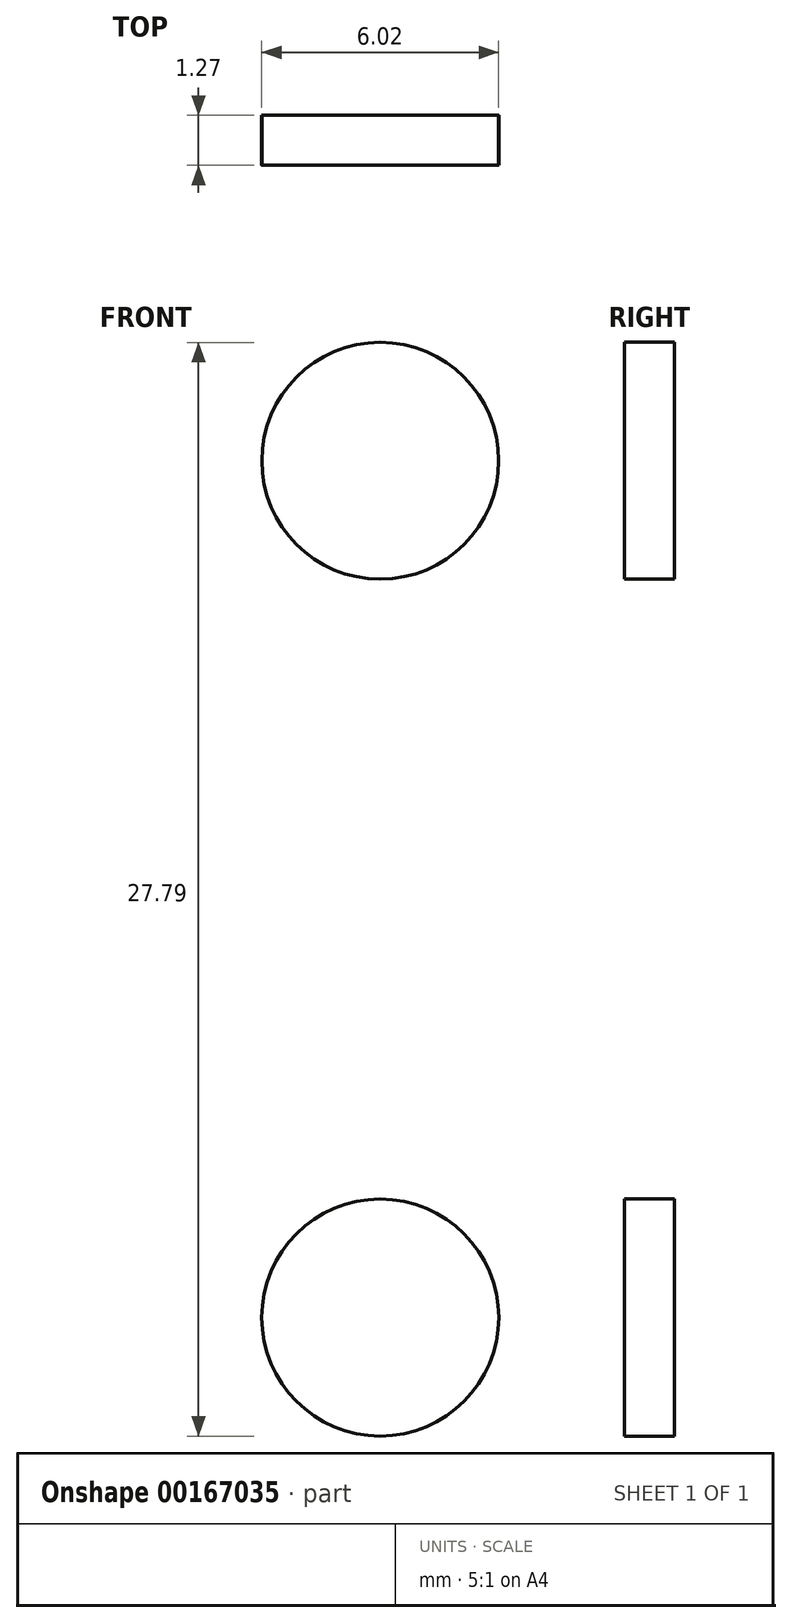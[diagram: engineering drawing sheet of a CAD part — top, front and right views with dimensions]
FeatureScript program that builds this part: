
annotation { "Feature Type Name" : "Feature", "Feature Type Description" : "" }
export const myFeature = defineFeature(function(context is Context, id is Id, definition is map)
    precondition{}
    {
        {
            var Q0;
            Q0=qCreatedBy(makeId("Front.planeOp"),FACE);
            var sketch = newSketch(context, id + "F0", { "sketchPlane" : qUnion([Q0])});
            skCircle(sketch, "E0", {"center": v(-32.4, 49.72) * mm, "radius": 3 * mm});
            skCircle(sketch, "E1", {"center": v(-32.4, 27.95) * mm, "radius": 3.01 * mm});
            skSolve(sketch);
        }
        {
            var Q0;
            Q0=makeQuery(id+"F0.imprint","IMPRINT",FACE,{"disambiguationData":[TD([[makeQuery(id+"F0.imprint","IMPRINT",EDGE,{"derivedFrom":sQuery(id+"F0.wireOp",EDGE,"E0")}),1.0]])]});
            var Q1;
            Q1=makeQuery(id+"F0.imprint","IMPRINT",FACE,{"disambiguationData":[TD([[makeQuery(id+"F0.imprint","IMPRINT",EDGE,{"derivedFrom":sQuery(id+"F0.wireOp",EDGE,"E1")}),1.0]])]});
            extrude(context, id + "F1", {"entities" : qUnion([Q0, Q1]), "depth" : 1.27 * mm});
        }
    });
